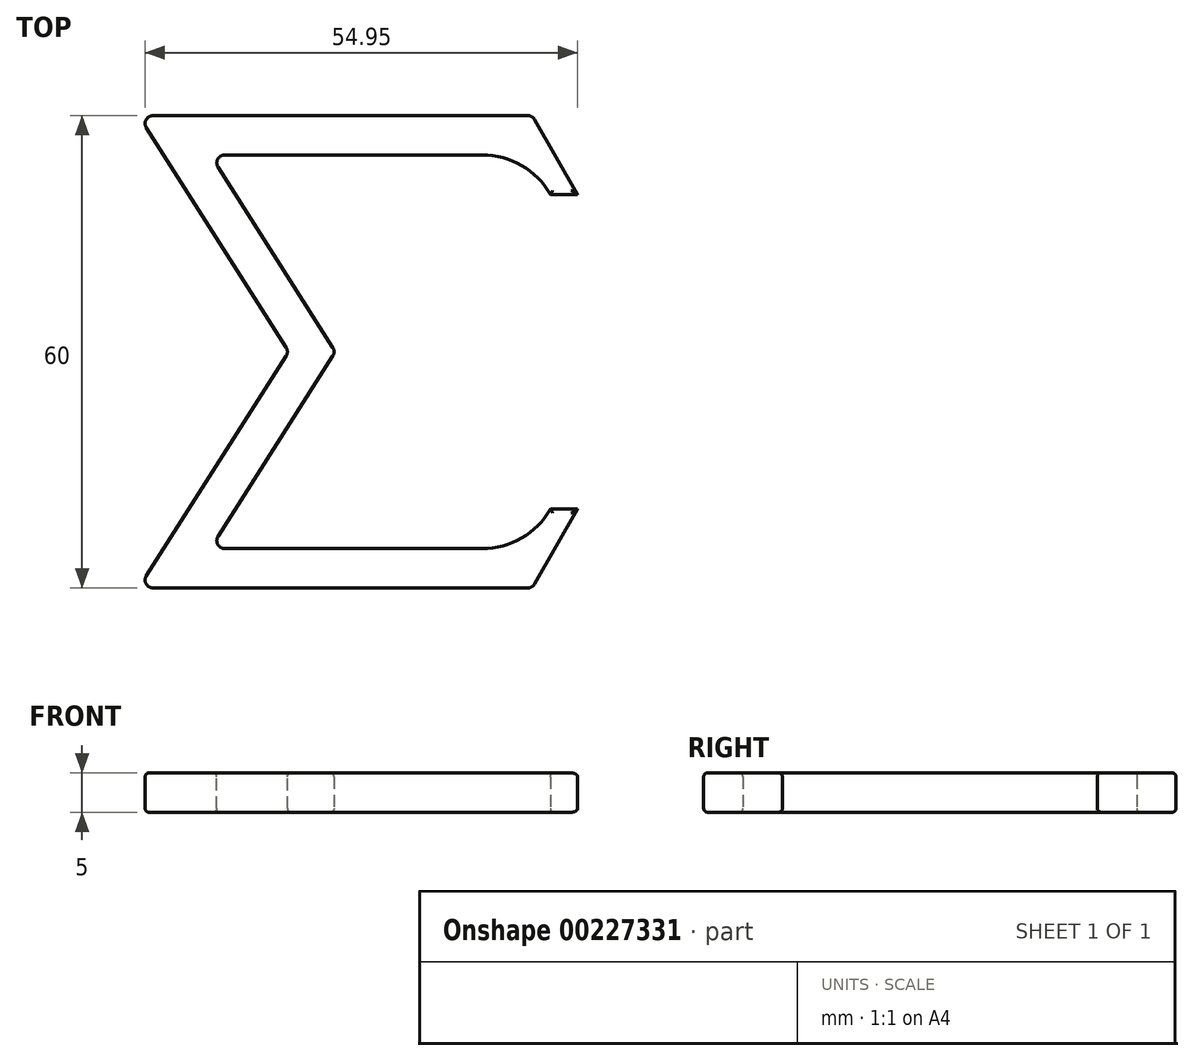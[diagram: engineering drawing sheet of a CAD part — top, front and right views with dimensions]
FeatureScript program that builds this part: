
annotation { "Feature Type Name" : "Feature", "Feature Type Description" : "" }
export const myFeature = defineFeature(function(context is Context, id is Id, definition is map)
    precondition{}
    {
        {
            var Q0;
            Q0=qCreatedBy(makeId("Top.planeOp"),FACE);
            var sketch = newSketch(context, id + "F0", { "sketchPlane" : qUnion([Q0])});
            skLineSegment(sketch, "E0", {"start": v(-25, 30) * mm, "end": v(25, 30) * mm});
            skLineSegment(sketch, "E1", {"start": v(25, 30) * mm, "end": v(30.77, 20) * mm});
            skLineSegment(sketch, "E2", {"start": v(30.77, 20) * mm, "end": v(27.3, 20) * mm});
            skLineSegment(sketch, "E3", {"start": v(27.3, 20) * mm, "end": v(24.42, 25) * mm});
            skLineSegment(sketch, "E4", {"start": v(24.42, 25) * mm, "end": v(-15.9, 25) * mm});
            skLineSegment(sketch, "E5", {"start": v(-15.9, 25) * mm, "end": v(0, 0) * mm});
            skLineSegment(sketch, "E6", {"start": v(0, 0) * mm, "end": v(-15.9, -25) * mm});
            skLineSegment(sketch, "E7", {"start": v(-15.9, -25) * mm, "end": v(24.42, -25) * mm});
            skLineSegment(sketch, "E8", {"start": v(24.42, -25) * mm, "end": v(27.3, -20) * mm});
            skLineSegment(sketch, "E9", {"start": v(27.3, -20) * mm, "end": v(30.77, -20) * mm});
            skLineSegment(sketch, "E10", {"start": v(30.77, -20) * mm, "end": v(25, -30) * mm});
            skLineSegment(sketch, "E11", {"start": v(25, -30) * mm, "end": v(-25, -30) * mm});
            skLineSegment(sketch, "E12", {"start": v(-25, -30) * mm, "end": v(-5.93, 0) * mm});
            skLineSegment(sketch, "E13", {"start": v(-5.93, 0) * mm, "end": v(-25, 30) * mm});
            skLineSegment(sketch, "E14", {"start": v(-25, -30) * mm, "end": v(-25, 30) * mm, "construction": true});
            skLineSegment(sketch, "E15", {"start": v(0, 0) * mm, "end": v(-25, 0) * mm, "construction": true});
            skSolve(sketch);
        }
        {
            var Q0;
            Q0 = qSketchRegion(id + "F0", true);
            extrude(context, id + "F1", {"entities" : qUnion([Q0]), "depth" : 5 * mm});
        }
        {
            var Q0;
            Q0=makeQuery(id+"F1.opExtrude","SWEPT_EDGE",EDGE,{"disambiguationData":[OSD([sQuery(id+"F0.wireOp",EDGE,"E3"),sQuery(id+"F0.wireOp",EDGE,"E4")])]});
            var Q1;
            Q1=makeQuery(id+"F1.opExtrude","SWEPT_EDGE",EDGE,{"disambiguationData":[OSD([sQuery(id+"F0.wireOp",EDGE,"E7"),sQuery(id+"F0.wireOp",EDGE,"E8")])]});
            fillet(context, id + "F2", {"entities" : qUnion([Q0, Q1]), "radius" : 10 * mm, "tangentPropagation" : true, "allowEdgeOverflow" : false});
        }
        {
            var Q0;
            Q0=makeQuery(id+"F1.opExtrude","SWEPT_EDGE",EDGE,{"disambiguationData":[OSD([sQuery(id+"F0.wireOp",EDGE,"E4"),sQuery(id+"F0.wireOp",EDGE,"E5")])]});
            var Q1;
            Q1=makeQuery(id+"F1.opExtrude","SWEPT_EDGE",EDGE,{"disambiguationData":[OSD([sQuery(id+"F0.wireOp",EDGE,"E6"),sQuery(id+"F0.wireOp",EDGE,"E7")])]});
            var Q2;
            Q2=makeQuery(id+"F1.opExtrude","SWEPT_EDGE",EDGE,{"disambiguationData":[OSD([sQuery(id+"F0.wireOp",EDGE,"E12"),sQuery(id+"F0.wireOp",EDGE,"E13")])]});
            fillet(context, id + "F3", {"entities" : qUnion([Q0, Q1, Q2]), "radius" : 1 * mm, "tangentPropagation" : true, "allowEdgeOverflow" : false});
        }
        {
            var Q0;
            Q0=makeQuery(id+"F1.opExtrude","SWEPT_EDGE",EDGE,{"disambiguationData":[OSD([sQuery(id+"F0.wireOp",EDGE,"E0"),sQuery(id+"F0.wireOp",EDGE,"E13")])]});
            var Q1;
            Q1=makeQuery(id+"F1.opExtrude","SWEPT_EDGE",EDGE,{"disambiguationData":[OSD([sQuery(id+"F0.wireOp",EDGE,"E5"),sQuery(id+"F0.wireOp",EDGE,"E6")])]});
            var Q2;
            Q2=makeQuery(id+"F1.opExtrude","SWEPT_EDGE",EDGE,{"disambiguationData":[OSD([sQuery(id+"F0.wireOp",EDGE,"E11"),sQuery(id+"F0.wireOp",EDGE,"E12")])]});
            var Q3;
            Q3=makeQuery(id+"F1.opExtrude","SWEPT_EDGE",EDGE,{"disambiguationData":[OSD([sQuery(id+"F0.wireOp",EDGE,"E10"),sQuery(id+"F0.wireOp",EDGE,"E11")])]});
            var Q4;
            Q4=makeQuery(id+"F1.opExtrude","SWEPT_EDGE",EDGE,{"disambiguationData":[OSD([sQuery(id+"F0.wireOp",EDGE,"E0"),sQuery(id+"F0.wireOp",EDGE,"E1")])]});
            fillet(context, id + "F4", {"entities" : qUnion([Q0, Q1, Q2, Q3, Q4]), "radius" : 1 * mm, "tangentPropagation" : true, "allowEdgeOverflow" : false});
        }
        {
            var Q0;
            Q0=makeQuery(id+"F1.opExtrude","CAP_FACE",FACE,{"disambiguationData":[OSD([sQuery(id+"F0.wireOp",EDGE,"E0"),sQuery(id+"F0.wireOp",EDGE,"E1"),sQuery(id+"F0.wireOp",EDGE,"E2"),sQuery(id+"F0.wireOp",EDGE,"E3"),sQuery(id+"F0.wireOp",EDGE,"E4"),sQuery(id+"F0.wireOp",EDGE,"E5"),sQuery(id+"F0.wireOp",EDGE,"E6"),sQuery(id+"F0.wireOp",EDGE,"E7"),sQuery(id+"F0.wireOp",EDGE,"E8"),sQuery(id+"F0.wireOp",EDGE,"E9"),sQuery(id+"F0.wireOp",EDGE,"E10"),sQuery(id+"F0.wireOp",EDGE,"E11"),sQuery(id+"F0.wireOp",EDGE,"E12"),sQuery(id+"F0.wireOp",EDGE,"E13")])],"isStart":false});
            var Q1;
            Q1=makeQuery(id+"F1.opExtrude","CAP_FACE",FACE,{"disambiguationData":[OSD([sQuery(id+"F0.wireOp",EDGE,"E0"),sQuery(id+"F0.wireOp",EDGE,"E1"),sQuery(id+"F0.wireOp",EDGE,"E2"),sQuery(id+"F0.wireOp",EDGE,"E3"),sQuery(id+"F0.wireOp",EDGE,"E4"),sQuery(id+"F0.wireOp",EDGE,"E5"),sQuery(id+"F0.wireOp",EDGE,"E6"),sQuery(id+"F0.wireOp",EDGE,"E7"),sQuery(id+"F0.wireOp",EDGE,"E8"),sQuery(id+"F0.wireOp",EDGE,"E9"),sQuery(id+"F0.wireOp",EDGE,"E10"),sQuery(id+"F0.wireOp",EDGE,"E11"),sQuery(id+"F0.wireOp",EDGE,"E12"),sQuery(id+"F0.wireOp",EDGE,"E13")])],"isStart":true});
            fillet(context, id + "F5", {"entities" : qUnion([Q0, Q1]), "radius" : .5 * mm, "tangentPropagation" : true, "allowEdgeOverflow" : false});
        }
    });
